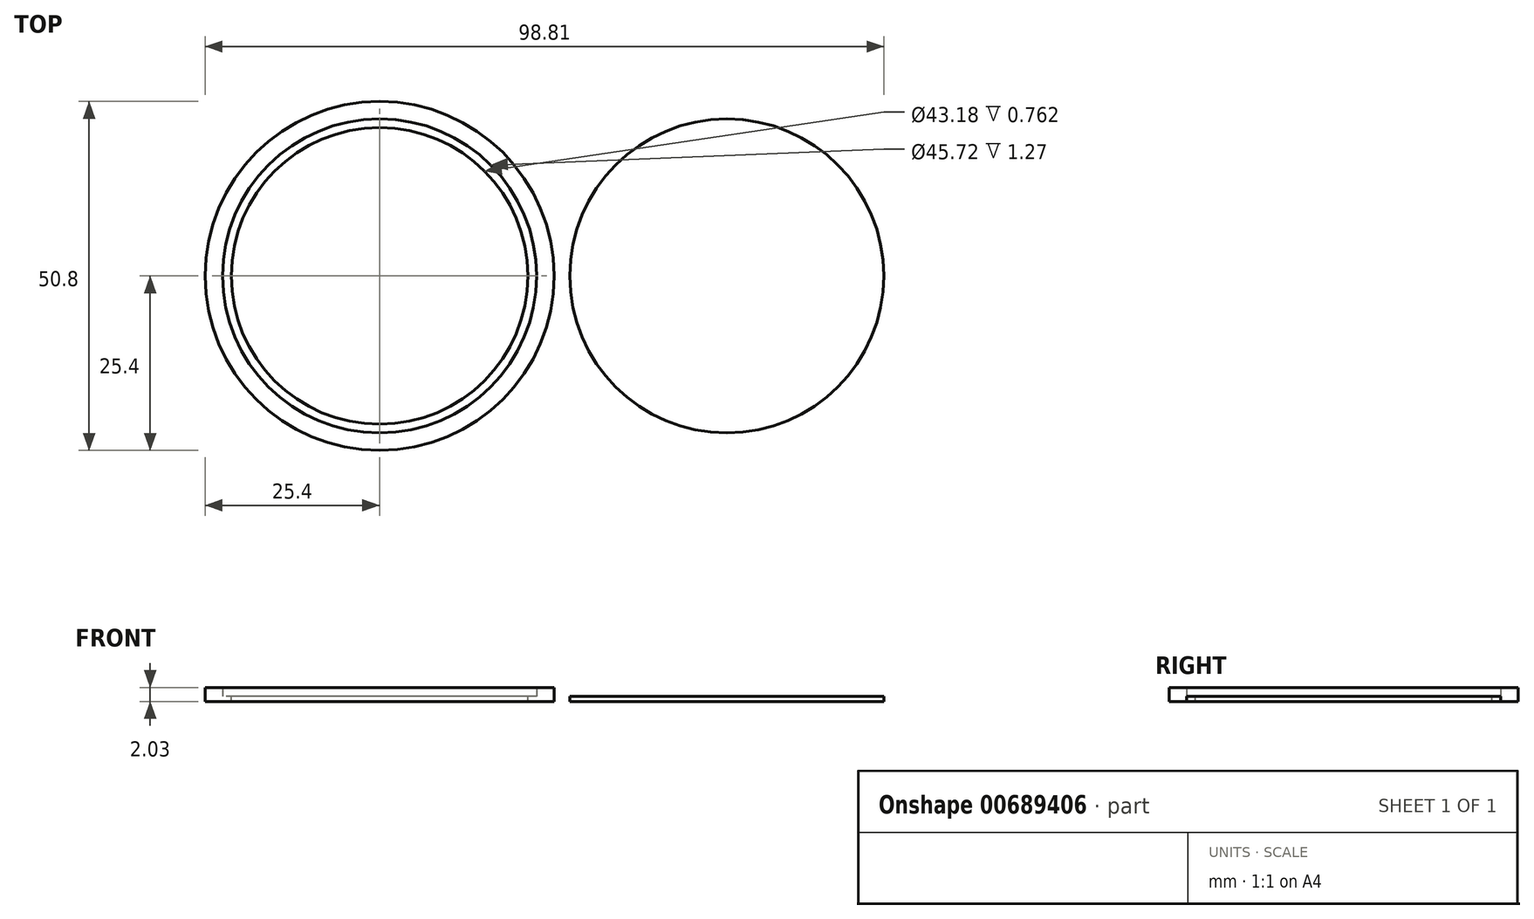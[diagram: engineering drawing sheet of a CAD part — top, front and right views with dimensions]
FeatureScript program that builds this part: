
annotation { "Feature Type Name" : "Feature", "Feature Type Description" : "" }
export const myFeature = defineFeature(function(context is Context, id is Id, definition is map)
    precondition{}
    {
        {
            var Q0;
            Q0=qCreatedBy(makeId("Top.planeOp"),FACE);
            var sketch = newSketch(context, id + "F0", { "sketchPlane" : qUnion([Q0])});
            skCircle(sketch, "E0", {"center": v(0, 0) * mm, "radius": 25.4 * mm});
            skCircle(sketch, "E1.0", {"center": v(0, 0) * mm, "radius": 22.86 * mm});
            skCircle(sketch, "E2.0", {"center": v(0, 0) * mm, "radius": 21.59 * mm});
            skLineSegment(sketch, "E3", {"start": v(0, 0) * mm, "end": v(-52.18, 0) * mm, "construction": true});
            skSolve(sketch);
        }
        {
            var Q0;
            Q0 = qSketchRegion(id + "F0", true);
            var Q1;
            Q1=makeQuery(id+"F0.imprint","IMPRINT",FACE,{"disambiguationData":[TD([[makeQuery(id+"F0.imprint","IMPRINT",EDGE,{"derivedFrom":sQuery(id+"F0.wireOp",EDGE,"E1.0")}),1.0]])]});
            extrude(context, id + "F1", {"entities" : qUnion([Q0, Q1]), "depth" : 0.76 * mm, "offsetDistance" : 25.4 * mm});
        }
        {
            var Q0;
            Q0 = qSketchRegion(id + "F0", true);
            extrude(context, id + "F2", {"entities" : qUnion([Q0]), "operationType" : NewBodyOperationType.ADD, "oppositeDirection" : true, "depth" : 1.27 * mm, "offsetDistance" : 25.4 * mm});
        }
        {
            var Q0;
            Q0=makeQuery(id+"F0.imprint","IMPRINT",FACE,{"disambiguationData":[TD([[makeQuery(id+"F0.imprint","IMPRINT",EDGE,{"derivedFrom":sQuery(id+"F0.wireOp",EDGE,"E2.0")}),1.0]])]});
            var Q1;
            Q1=makeQuery(id+"F0.imprint","IMPRINT",FACE,{"disambiguationData":[TD([[makeQuery(id+"F0.imprint","IMPRINT",EDGE,{"derivedFrom":sQuery(id+"F0.wireOp",EDGE,"E1.0")}),1.0]])]});
            extrude(context, id + "F3", {"entities" : qUnion([Q0, Q1]), "oppositeDirection" : true, "depth" : 0.76 * mm, "offsetDistance" : 25.4 * mm});
        }
        {
            var Q0;
            Q0=makeQuery(id+"F3.opExtrude","SWEPT_BODY",BODY,{"disambiguationData":[OSD([sQuery(id+"F0.wireOp",EDGE,"E1.0")])]});
            transform(context, id + "F4", {"entities" : qUnion([Q0]), "transformType" : TransformType.TRANSLATION_3D, "dx" : 50.55 * mm, "dy" : 0 * mm, "dz" : 0 * mm, "makeCopy" : false});
        }
        {
            var Q0;
            Q0=makeQuery(id+"F1.opExtrude","SWEPT_BODY",BODY,{"disambiguationData":[OSD([sQuery(id+"F0.wireOp",EDGE,"E0"),sQuery(id+"F0.wireOp",EDGE,"E2.0")])]});
            var Q1;
            Q1=sQuery(id+"F0.wireOp",EDGE,"E3");
            transform(context, id + "F5", {"entities" : qUnion([Q0]), "transformType" : TransformType.ROTATION, "transformAxis" : qUnion([Q1]), "angle" : 180 * degree, "makeCopy" : false});
        }
    });
